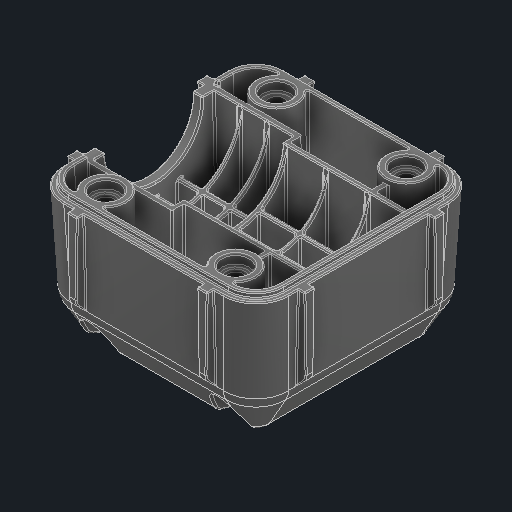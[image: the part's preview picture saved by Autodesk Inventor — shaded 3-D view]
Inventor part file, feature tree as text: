
AUTODESK INVENTOR PART (.ipt)
format: ipt  version: 2025 (Build 290162000, 162)  size: 2,869,760 bytes
history: native  units: in
note: dims shown in document units (in); Inventor stores cm internally (conversion verified against a paired STEP export)
features: fillet x1
ambient origin geometry x8: Origin, YZ Plane, XZ Plane, XY Plane, X Axis, Y Axis, Z Axis, Center Point
bodies: Solid1 (feature_tree)
feature tree (1):
  fillet  "Fillet32"  [1 undecoded]
note: 1 required parameter value undecoded (feature->parameter linkage not recoverable at this tier; creation-order binding heuristic only, values carry confidence <= 0.55)
